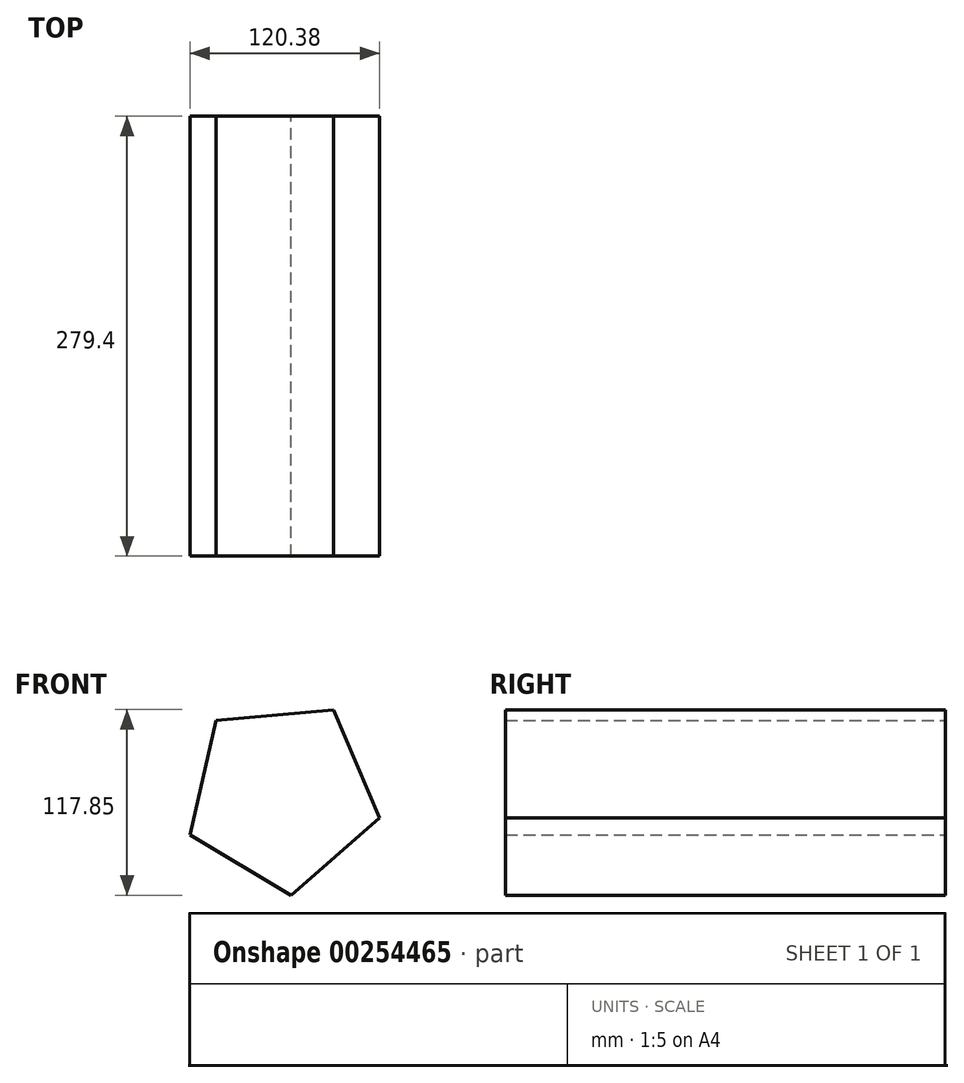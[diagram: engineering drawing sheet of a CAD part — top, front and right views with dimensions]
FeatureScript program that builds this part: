
annotation { "Feature Type Name" : "Feature", "Feature Type Description" : "" }
export const myFeature = defineFeature(function(context is Context, id is Id, definition is map)
    precondition{}
    {
        {
            var Q0;
            Q0=qCreatedBy(makeId("Front.planeOp"),FACE);
            var sketch = newSketch(context, id + "F0", { "sketchPlane" : qUnion([Q0])});
            skCircle(sketch, "E0.cCircle", {"center": v(-52.43, 53.19) * mm, "radius": 51.41 * mm, "construction": true});
            skLineSegment(sketch, "E0.0", {"start": v(9.53, 39.06) * mm, "end": v(-46.72, -10.1) * mm});
            skLineSegment(sketch, "E0.1", {"start": v(-46.72, -10.1) * mm, "end": v(-110.85, 28.2) * mm});
            skLineSegment(sketch, "E0.2", {"start": v(-110.85, 28.2) * mm, "end": v(-94.25, 101.04) * mm});
            skLineSegment(sketch, "E0.3", {"start": v(-94.25, 101.04) * mm, "end": v(-19.84, 107.75) * mm});
            skLineSegment(sketch, "E0.4", {"start": v(-19.84, 107.75) * mm, "end": v(9.53, 39.06) * mm});
            skPoint(sketch, "E0.0.midPoint", {"position": v(-18.6, 14.48) * mm});
            skSolve(sketch);
        }
        {
            var Q0;
            Q0=makeQuery(id+"F0.imprint","IMPRINT",FACE,{"disambiguationData":[TD([[makeQuery(id+"F0.imprint","IMPRINT",EDGE,{"derivedFrom":sQuery(id+"F0.wireOp",EDGE,"E0.0")}),-1.0]])]});
            extrude(context, id + "F1", {"entities" : qUnion([Q0]), "depth" : 279.4 * mm});
        }
    });
